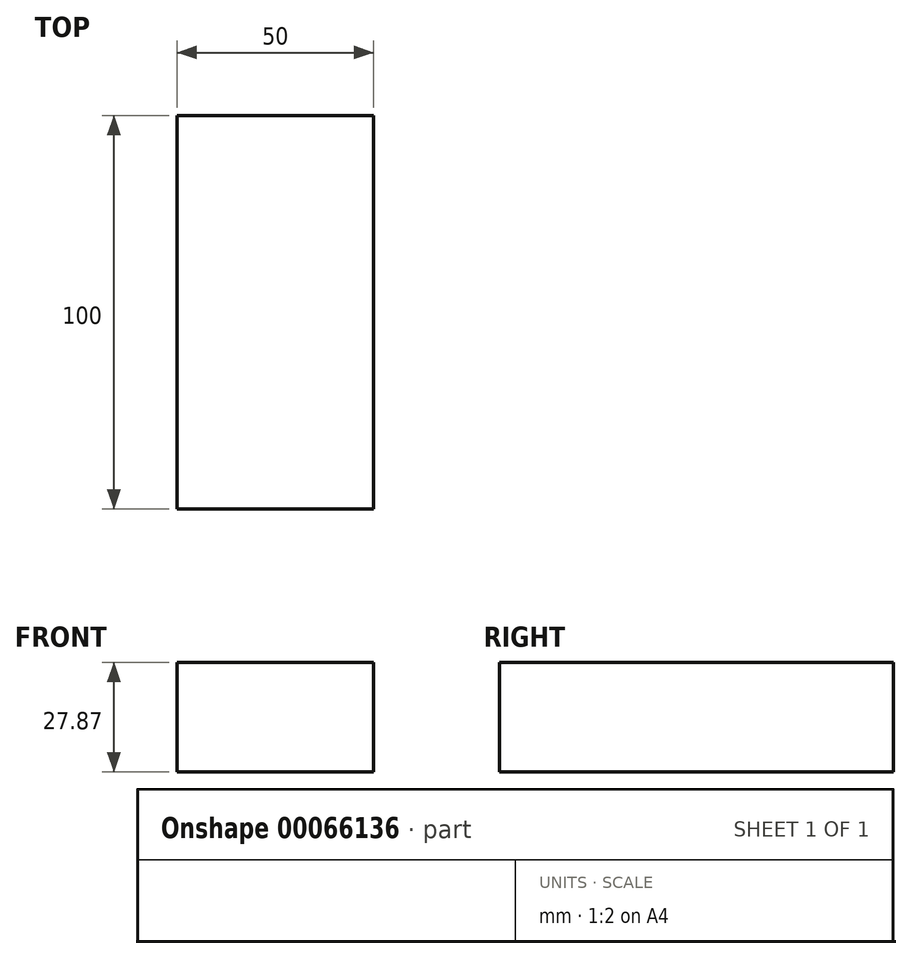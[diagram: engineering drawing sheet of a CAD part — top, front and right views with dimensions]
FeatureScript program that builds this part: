
annotation { "Feature Type Name" : "Feature", "Feature Type Description" : "" }
export const myFeature = defineFeature(function(context is Context, id is Id, definition is map)
    precondition{}
    {
        {
            var Q0;
            Q0=qCreatedBy(makeId("Front.planeOp"),FACE);
            var sketch = newSketch(context, id + "F0", { "sketchPlane" : qUnion([Q0])});
            skLineSegment(sketch, "E0", {"start": v(-29.5, 0) * mm, "end": v(0, 29.55) * mm});
            skLineSegment(sketch, "E1", {"start": v(0, 29.55) * mm, "end": v(0, 52.1) * mm});
            skLineSegment(sketch, "E2", {"start": v(0, 52.1) * mm, "end": v(-50.8, 0) * mm});
            skLineSegment(sketch, "E3", {"start": v(-50.8, 0) * mm, "end": v(-29.5, 0) * mm});
            skCircle(sketch, "E4", {"center": v(29.93, 34.06) * mm, "radius": 15.36 * mm});
            skLineSegment(sketch, "E5.rect.bottom", {"start": v(-9.83, -45.86) * mm, "end": v(-59.83, -45.86) * mm});
            skLineSegment(sketch, "E5.rect.top", {"start": v(-9.83, -18) * mm, "end": v(-59.83, -18) * mm});
            skLineSegment(sketch, "E5.rect.left", {"start": v(-9.83, -45.86) * mm, "end": v(-9.83, -18) * mm});
            skLineSegment(sketch, "E5.rect.right", {"start": v(-59.83, -45.86) * mm, "end": v(-59.83, -18) * mm});
            skPoint(sketch, "E5.rect.middle", {"position": v(-34.83, -31.93) * mm});
            skSolve(sketch);
        }
        {
            var Q0;
            Q0 = qSketchRegion(id + "F0", true);
            extrude(context, id + "F1", {"entities" : qUnion([Q0]), "depth" : 100 * mm});
        }
        {
            var Q0;
            Q0=makeQuery(id+"F1.opExtrude","SWEPT_BODY",BODY,{"disambiguationData":[OSD([sQuery(id+"F0.wireOp",EDGE,"E0"),sQuery(id+"F0.wireOp",EDGE,"E1"),sQuery(id+"F0.wireOp",EDGE,"E2"),sQuery(id+"F0.wireOp",EDGE,"E3")])]});
            var Q1;
            Q1=makeQuery(id+"F1.opExtrude","SWEPT_BODY",BODY,{"disambiguationData":[OSD([sQuery(id+"F0.wireOp",EDGE,"E4")])]});
            deleteBodies(context, id + "F2", {"entities" : qUnion([Q0, Q1])});
        }
    });
